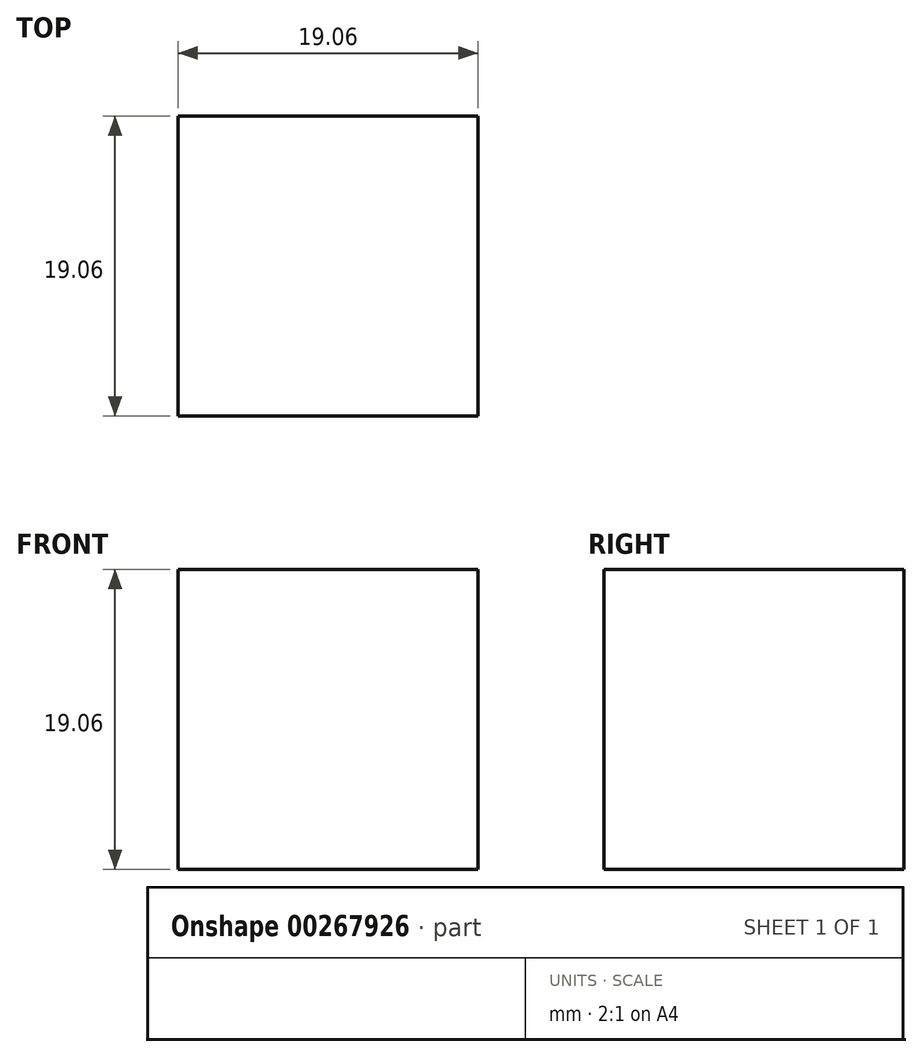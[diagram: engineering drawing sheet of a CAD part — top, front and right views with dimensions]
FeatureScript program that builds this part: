
annotation { "Feature Type Name" : "Feature", "Feature Type Description" : "" }
export const myFeature = defineFeature(function(context is Context, id is Id, definition is map)
    precondition{}
    {
        {
            var Q0;
            Q0=qCreatedBy(makeId("Front.planeOp"),FACE);
            var sketch = newSketch(context, id + "F0", { "sketchPlane" : qUnion([Q0])});
            skLineSegment(sketch, "E0.bottom", {"start": v(-9.53, 9.52) * mm, "end": v(9.52, 9.52) * mm});
            skLineSegment(sketch, "E0.top", {"start": v(-9.53, -9.53) * mm, "end": v(9.52, -9.53) * mm});
            skLineSegment(sketch, "E0.left", {"start": v(-9.53, 9.52) * mm, "end": v(-9.53, -9.53) * mm});
            skLineSegment(sketch, "E0.right", {"start": v(9.52, 9.52) * mm, "end": v(9.52, -9.53) * mm});
            skPoint(sketch, "E0.middle", {"position": v(0, 0) * mm});
            skSolve(sketch);
        }
        {
            var Q0;
            Q0 = qSketchRegion(id + "F0", true);
            extrude(context, id + "F1", {"entities" : qUnion([Q0]), "endBound" : BoundingType.SYMMETRIC, "depth" : 19.05 * mm});
        }
    });
